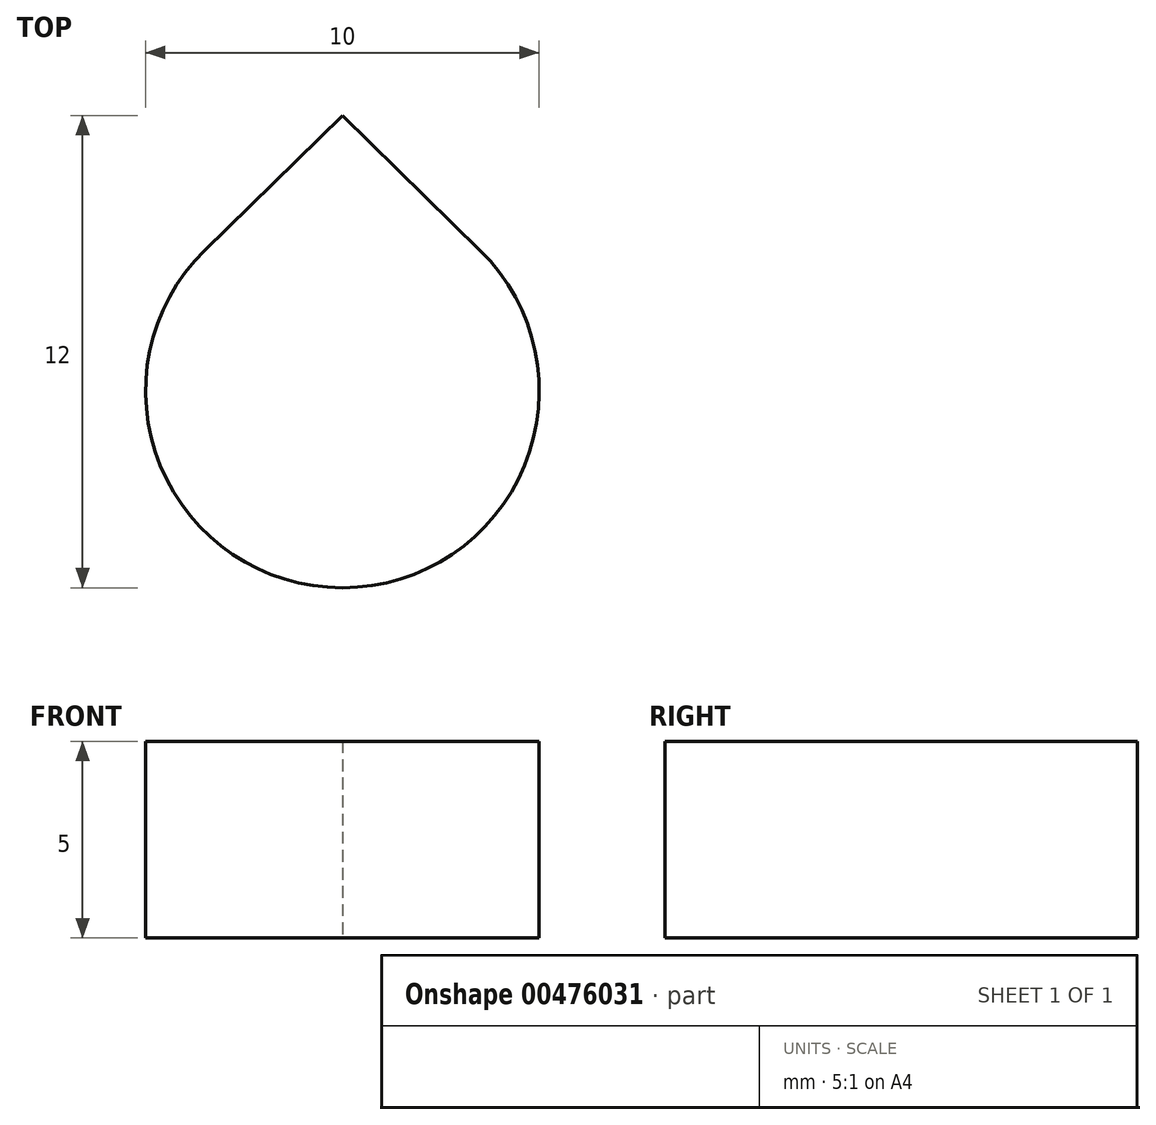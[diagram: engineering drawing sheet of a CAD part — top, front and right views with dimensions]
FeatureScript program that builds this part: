
annotation { "Feature Type Name" : "Feature", "Feature Type Description" : "" }
export const myFeature = defineFeature(function(context is Context, id is Id, definition is map)
    precondition{}
    {
        {
            var Q0;
            Q0=qCreatedBy(makeId("Top.planeOp"),FACE);
            var sketch = newSketch(context, id + "F0", { "sketchPlane" : qUnion([Q0])});
            skArc(sketch, "E0", {"start": v(-3.5, 3.57) * mm, "mid": v(0, -5) * mm, "end": v(3.5, 3.57) * mm});
            skLineSegment(sketch, "E1", {"start": v(-3.5, 3.57) * mm, "end": v(0, 7) * mm});
            skLineSegment(sketch, "E2", {"start": v(0, 7) * mm, "end": v(3.5, 3.57) * mm});
            skSolve(sketch);
        }
        {
            var Q0;
            Q0 = qSketchRegion(id + "F0", true);
            extrude(context, id + "F1", {"entities" : qUnion([Q0]), "depth" : 5 * mm});
        }
    });
